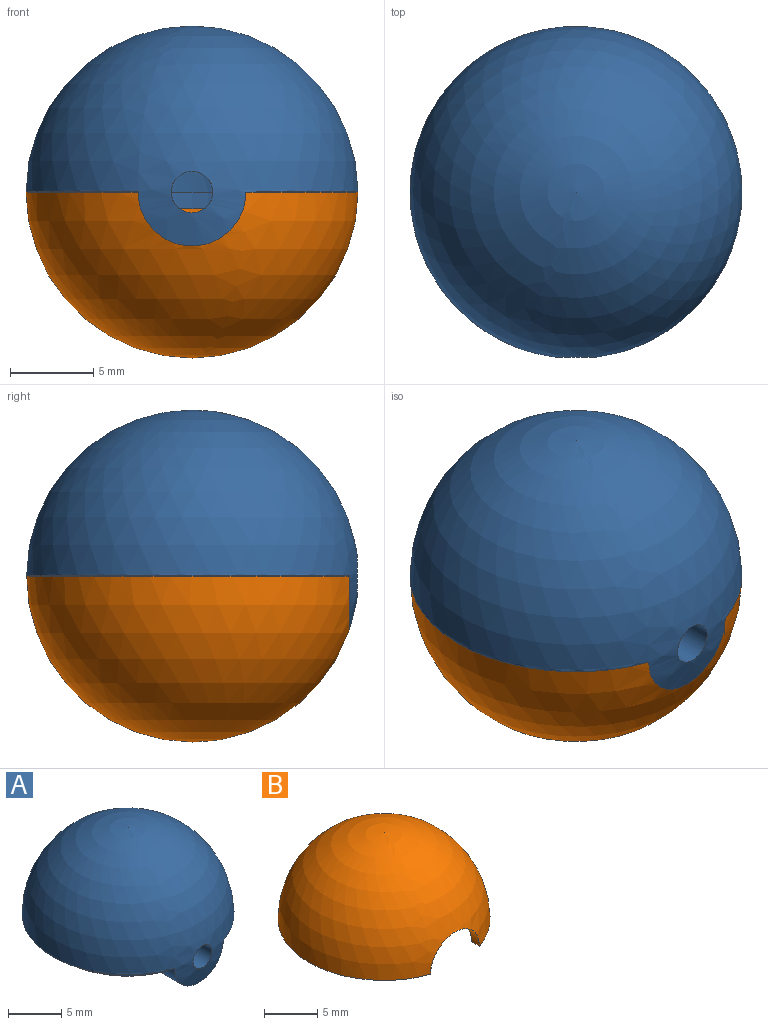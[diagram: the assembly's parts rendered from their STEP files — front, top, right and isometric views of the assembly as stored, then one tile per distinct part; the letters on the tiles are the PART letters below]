
ASSEMBLY  parts=2 mates=1
PART A: 9 faces, bbox 20x20x13.3 mm
  f0: sphere r=10mm, area 640.4mm2, adj f1,f6,f8
  f1: plane 20x19.46mm, normal (0,0,-1), area 62.9mm2, adj f0,f2,f6
  f2: cylinder r=8.8mm len=17.6mm, axis (0,0,-1), area 48.7mm2, adj f1,f3,f6
  f3: plane 17.6x17.04mm, normal (0,0,-1), area 37.2mm2, adj f2,f4,f6
  f4: cylinder r=8mm len=16mm, axis (0,0,-1), area 43.7mm2, adj f3,f5,f6
  f5: sphere r=8mm, area 384.8mm2, adj f4,f6
  f6: cylinder r=3.25mm len=9.46mm, axis (0,1,0), area 169.4mm2, adj f0,f1,f2,f3,f4,f5,f7
  f7: plane 6.5x6.5mm, normal (0,1,0), area 28.3mm2, adj f6,f8
  f8: cylinder r=1.25mm len=9.92mm, axis (0,1,0), area 77.9mm2, adj f0,f7
PART B: 6 faces, bbox 20x20x10 mm
  f0: plane 20x19.46mm, normal (0,0,-1), area 53.1mm2, adj f1,f4,f5
  f1: cylinder r=9mm len=18mm, axis (0,0,-1), area 100.7mm2, adj f0,f2,f5
  f2: plane 18x17.63mm, normal (0,0,-1), area 59.4mm2, adj f1,f3,f5
  f3: sphere r=8mm, area 296.8mm2, adj f2,f5
  f4: sphere r=10mm, area 611.3mm2, adj f0,f5
  f5: cylinder r=3.25mm len=6.5mm, axis (0,1,0), area 16.9mm2, adj f0,f1,f2,f3,f4
PLACE A t=(7.39,-15.47,0)mm
PLACE B rot(axis=(0,1,0),180deg) t=(7.39,-15.47,0)mm
MATE ball B.f1 <-> A.f2  axis (0,0,1) through (7.39,-15.47,0)mm
